# Revit family: OP-1000-1000
name_source: partatom
category: Generic Models
revit_build: Autodesk Revit 2017 (Build: 20171027_0315(x64)
units: mm (PartAtom-declared; Revit-internal decimal feet)

## family parameters
Always vertical = No
Can host rebar = No
Cut with Voids When Loaded = No
Host = Floor
Part Type = Normal
Room Calculation Point = No
Round Connector Dimension = Use Diameter
Shared = Yes

## types (4) — shared parameters
Belastbaarheid = 5 kN/m² volgens NEN-EN1991
Bevestiging = Verankering opgenomen in frame
C = 400 mm  [stored 1.31234 ft]
Model = OP
Speciale afmeting = Speciale afmetingen zijn leverbaar.
URL = https://www.gortergroup.com
frame = geanodiseerd aluminium frame
vloerluik = geanodiseerd aluminium tranenplaat

## per-type parameters (varying)
| type | A | B | OP-Ankerpunten afstand | Weight (kg) |
| OP-800-800 | 800 mm  [stored 2.62467 ft] | 800 mm  [stored 2.62467 ft] | 250 mm  [stored 0.82021 ft] | 20 |
| OP-1000-1000 | 1000 mm  [stored 3.28084 ft] | 1000 mm  [stored 3.28084 ft] | 250 mm  [stored 0.82021 ft] | 27 |
| OP-1000-1500 | 1500 mm  [stored 4.92126 ft] | 1000 mm  [stored 3.28084 ft] | 300 mm  [stored 0.984252 ft] | 44 |
| OP-1000-2000 | 2000 mm  [stored 6.56168 ft] | 1000 mm  [stored 3.28084 ft] | 300 mm  [stored 0.984252 ft] | 57 |

type visibility flags: 4 boolean params named "<type name>" — each type sets only its own to Yes (folded from table)

note: [stored X ft] marks values corroborated as IEEE doubles in the binary element streams (Revit-internal decimal feet)

## geometry (parser evidence)
native form markers: Sweep x12
no freeform markers — native parametric forms only
